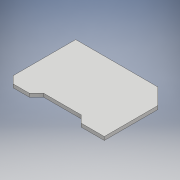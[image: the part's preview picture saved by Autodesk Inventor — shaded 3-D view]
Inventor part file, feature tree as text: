
AUTODESK INVENTOR PART (.ipt)
format: ipt  version: 2018 (Build 220112000, 112)  size: 104,448 bytes
history: native  units: mm
features: extrude x1, sketch x1
ambient origin geometry x8: Origin, YZ Plane, XZ Plane, XY Plane, X Axis, Y Axis, Z Axis, Center Point
bodies: Solid1 (feature_tree)
feature tree (2):
  extrude  "Extrusion1"  Depth=39.0mm
  sketch  "Sketch1"  dims[d0=55.0mm d1=39.0mm d2=9.0mm d3=9.0mm d4=4.0mm d5=4.0mm d6=1.91mm d7=0.0mm d11=17.0mm d12=17.0mm]
